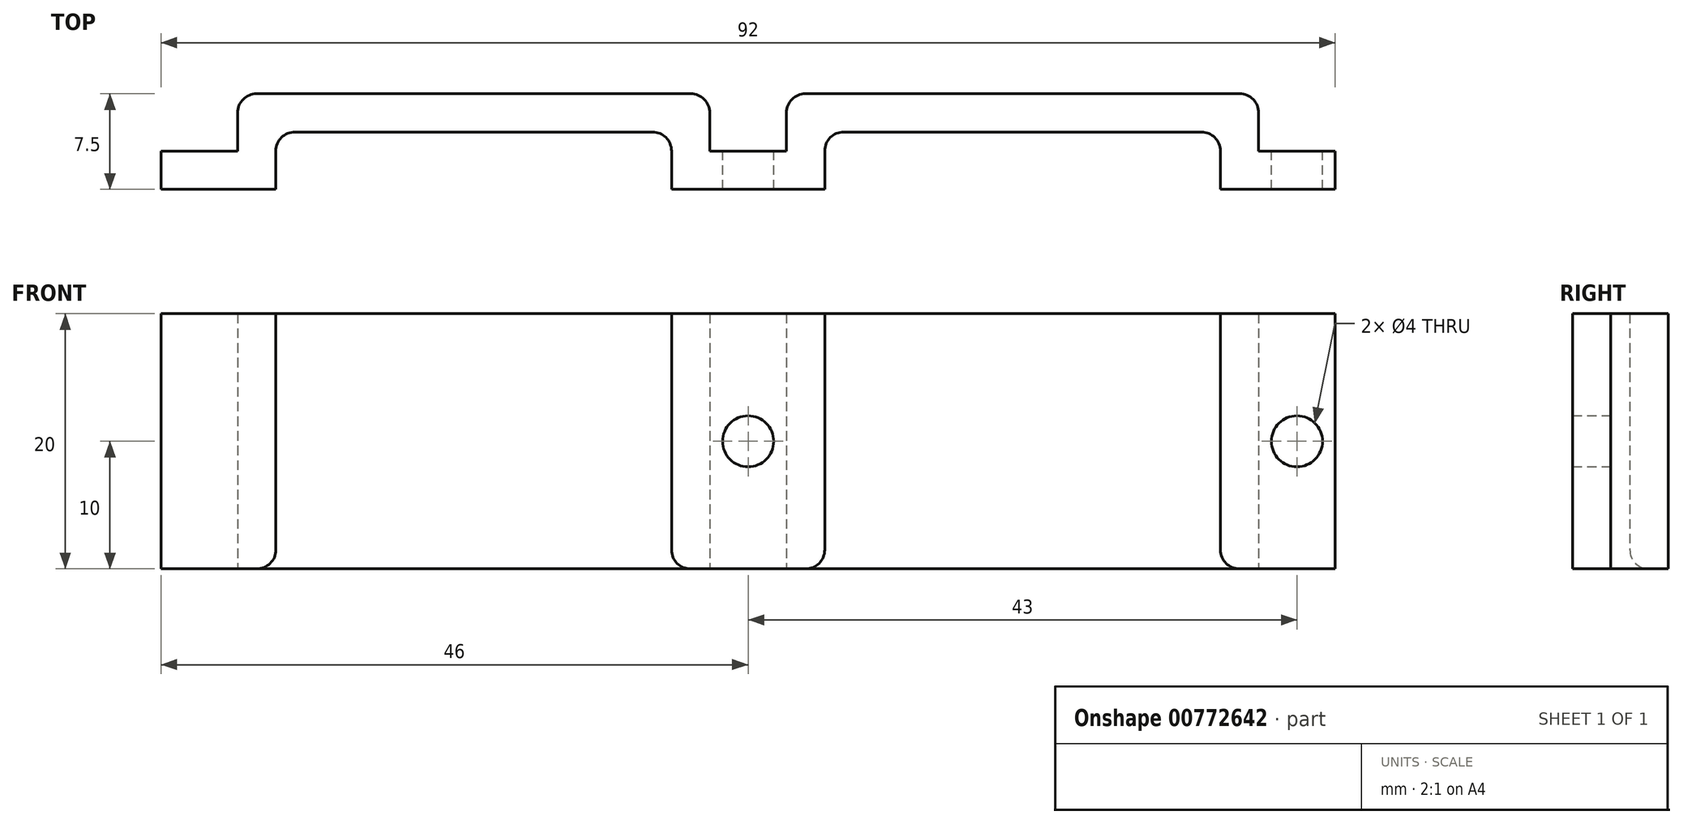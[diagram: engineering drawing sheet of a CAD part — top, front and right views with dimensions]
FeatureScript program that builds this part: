
annotation { "Feature Type Name" : "Feature", "Feature Type Description" : "" }
export const myFeature = defineFeature(function(context is Context, id is Id, definition is map)
    precondition{}
    {
        {
            var Q0;
            Q0=qCreatedBy(makeId("Top.planeOp"),FACE);
            var sketch = newSketch(context, id + "F0", { "sketchPlane" : qUnion([Q0])});
            skPoint(sketch, "E0.middle", {"position": v(0, 0) * mm});
            skLineSegment(sketch, "E1", {"start": v(-37, -4) * mm, "end": v(-37, 0.5) * mm});
            skLineSegment(sketch, "E2", {"start": v(-37, 0.5) * mm, "end": v(-6, 0.5) * mm});
            skLineSegment(sketch, "E3", {"start": v(-6, 0.5) * mm, "end": v(-6, -4) * mm});
            skLineSegment(sketch, "E4", {"start": v(-3, -1) * mm, "end": v(0, -1) * mm});
            skLineSegment(sketch, "E5", {"start": v(-40, -4) * mm, "end": v(-46, -4) * mm});
            skLineSegment(sketch, "E6", {"start": v(-46, -4) * mm, "end": v(-46, -1) * mm});
            skLineSegment(sketch, "E7", {"start": v(-46, -1) * mm, "end": v(-40, -1) * mm});
            skLineSegment(sketch, "E8", {"start": v(-40, -1) * mm, "end": v(-40, 3.5) * mm});
            skLineSegment(sketch, "E9", {"start": v(-40, 3.5) * mm, "end": v(-3, 3.5) * mm});
            skLineSegment(sketch, "E10", {"start": v(-3, -1) * mm, "end": v(-3, 3.5) * mm});
            skPoint(sketch, "E11.orphan", {"position": v(0, 3.5) * mm});
            skLineSegment(sketch, "E12.trimOffspring", {"start": v(-37, -4) * mm, "end": v(-40, -4) * mm});
            skLineSegment(sketch, "E13.MirrorCS", {"start": v(3, -1) * mm, "end": v(0, -1) * mm});
            skLineSegment(sketch, "E14.MirrorCS", {"start": v(3, -1) * mm, "end": v(3, 3.5) * mm});
            skLineSegment(sketch, "E15.MirrorCS", {"start": v(40, 3.5) * mm, "end": v(3, 3.5) * mm});
            skLineSegment(sketch, "E16.MirrorCS", {"start": v(40, -1) * mm, "end": v(40, 3.5) * mm});
            skLineSegment(sketch, "E17.MirrorCS", {"start": v(46, -1) * mm, "end": v(40, -1) * mm});
            skLineSegment(sketch, "E18.MirrorCS", {"start": v(46, -4) * mm, "end": v(46, -1) * mm});
            skLineSegment(sketch, "E19.MirrorCS", {"start": v(40, -4) * mm, "end": v(46, -4) * mm});
            skLineSegment(sketch, "E20.MirrorCS", {"start": v(37, -4) * mm, "end": v(40, -4) * mm});
            skLineSegment(sketch, "E21.MirrorCS", {"start": v(37, -4) * mm, "end": v(37, 0.5) * mm});
            skLineSegment(sketch, "E22.MirrorCS", {"start": v(37, 0.5) * mm, "end": v(6, 0.5) * mm});
            skLineSegment(sketch, "E23.MirrorCS", {"start": v(6, 0.5) * mm, "end": v(6, -4) * mm});
            skLineSegment(sketch, "E24", {"start": v(-6, -4) * mm, "end": v(6, -4) * mm});
            skSolve(sketch);
        }
        {
            var Q0;
            Q0=makeQuery(id+"F0.imprint","IMPRINT",FACE,{"disambiguationData":[TD([[makeQuery(id+"F0.imprint","IMPRINT",EDGE,{"derivedFrom":sQuery(id+"F0.wireOp",EDGE,"E1")}),1.0]])]});
            extrude(context, id + "F1", {"entities" : qUnion([Q0]), "depth" : 20 * mm, "offsetDistance" : 25 * mm});
        }
        {
            var Q0;
            Q0=makeQuery(id+"F1.opExtrude","CAP_EDGE",EDGE,{"disambiguationData":[OSD([sQuery(id+"F0.wireOp",EDGE,"E2")])],"isStart":true});
            var Q1;
            Q1=makeQuery(id+"F1.opExtrude","CAP_EDGE",EDGE,{"disambiguationData":[OSD([sQuery(id+"F0.wireOp",EDGE,"E1")])],"isStart":true});
            var Q2;
            Q2=makeQuery(id+"F1.opExtrude","CAP_EDGE",EDGE,{"disambiguationData":[OSD([sQuery(id+"F0.wireOp",EDGE,"E3")])],"isStart":true});
            var Q3;
            Q3=makeQuery(id+"F1.opExtrude","CAP_EDGE",EDGE,{"disambiguationData":[OSD([sQuery(id+"F0.wireOp",EDGE,"E23.MirrorCS")])],"isStart":true});
            var Q4;
            Q4=makeQuery(id+"F1.opExtrude","CAP_EDGE",EDGE,{"disambiguationData":[OSD([sQuery(id+"F0.wireOp",EDGE,"E22.MirrorCS")])],"isStart":true});
            var Q5;
            Q5=makeQuery(id+"F1.opExtrude","CAP_EDGE",EDGE,{"disambiguationData":[OSD([sQuery(id+"F0.wireOp",EDGE,"E21.MirrorCS")])],"isStart":true});
            var Q6;
            Q6=makeQuery(id+"F1.opExtrude","SWEPT_EDGE",EDGE,{"disambiguationData":[OSD([sQuery(id+"F0.wireOp",EDGE,"E8"),sQuery(id+"F0.wireOp",EDGE,"E9")])]});
            var Q7;
            Q7=makeQuery(id+"F1.opExtrude","SWEPT_EDGE",EDGE,{"disambiguationData":[OSD([sQuery(id+"F0.wireOp",EDGE,"E9"),sQuery(id+"F0.wireOp",EDGE,"E10")])]});
            var Q8;
            Q8=makeQuery(id+"F1.opExtrude","SWEPT_EDGE",EDGE,{"disambiguationData":[OSD([sQuery(id+"F0.wireOp",EDGE,"E14.MirrorCS"),sQuery(id+"F0.wireOp",EDGE,"E15.MirrorCS")])]});
            var Q9;
            Q9=makeQuery(id+"F1.opExtrude","SWEPT_EDGE",EDGE,{"disambiguationData":[OSD([sQuery(id+"F0.wireOp",EDGE,"E15.MirrorCS"),sQuery(id+"F0.wireOp",EDGE,"E16.MirrorCS")])]});
            var Q10;
            Q10=makeQuery(id+"F1.opExtrude","SWEPT_EDGE",EDGE,{"disambiguationData":[OSD([sQuery(id+"F0.wireOp",EDGE,"E1"),sQuery(id+"F0.wireOp",EDGE,"E2")])]});
            var Q11;
            Q11=makeQuery(id+"F1.opExtrude","SWEPT_EDGE",EDGE,{"disambiguationData":[OSD([sQuery(id+"F0.wireOp",EDGE,"E2"),sQuery(id+"F0.wireOp",EDGE,"E3")])]});
            var Q12;
            Q12=makeQuery(id+"F1.opExtrude","SWEPT_EDGE",EDGE,{"disambiguationData":[OSD([sQuery(id+"F0.wireOp",EDGE,"E22.MirrorCS"),sQuery(id+"F0.wireOp",EDGE,"E23.MirrorCS")])]});
            var Q13;
            Q13=makeQuery(id+"F1.opExtrude","SWEPT_EDGE",EDGE,{"disambiguationData":[OSD([sQuery(id+"F0.wireOp",EDGE,"E21.MirrorCS"),sQuery(id+"F0.wireOp",EDGE,"E22.MirrorCS")])]});
            fillet(context, id + "F2", {"entities" : qUnion([Q0, Q1, Q2, Q3, Q4, Q5, Q6, Q7, Q8, Q9, Q10, Q11, Q12, Q13]), "radius" : 1.5 * mm, "tangentPropagation" : true, "allowEdgeOverflow" : false});
        }
        {
            var Q0;
            Q0=makeQuery(id+"F1.opExtrude","SWEPT_FACE",FACE,{"disambiguationData":[OSD([sQuery(id+"F0.wireOp",EDGE,"E4"),sQuery(id+"F0.wireOp",EDGE,"E13.MirrorCS")])]});
            var sketch = newSketch(context, id + "F3", { "sketchPlane" : qUnion([Q0])});
            skCircle(sketch, "E25", {"center": v(0, 10) * mm, "radius": 2 * mm});
            skCircle(sketch, "E26", {"center": v(-43, 10) * mm, "radius": 2 * mm});
            skCircle(sketch, "E27.MirrorC", {"center": v(43, 10) * mm, "radius": 2 * mm});
            skSolve(sketch);
        }
        {
            var Q0;
            Q0=makeQuery(id+"F3.imprint","IMPRINT",FACE,{"disambiguationData":[TD([[makeQuery(id+"F3.imprint","IMPRINT",EDGE,{"derivedFrom":sQuery(id+"F3.wireOp",EDGE,"E26")}),1.0]])]});
            var Q1;
            Q1=makeQuery(id+"F3.imprint","IMPRINT",FACE,{"disambiguationData":[TD([[makeQuery(id+"F3.imprint","IMPRINT",EDGE,{"derivedFrom":sQuery(id+"F3.wireOp",EDGE,"E25")}),1.0]])]});
            var Q2;
            Q2=makeQuery(id+"F3.imprint","IMPRINT",FACE,{"disambiguationData":[TD([[makeQuery(id+"F3.imprint","IMPRINT",EDGE,{"derivedFrom":sQuery(id+"F3.wireOp",EDGE,"E27.MirrorC")}),-1.0]])]});
            extrude(context, id + "F4", {"entities" : qUnion([Q0, Q1, Q2]), "operationType" : NewBodyOperationType.REMOVE, "oppositeDirection" : true, "depth" : 25 * mm, "offsetDistance" : 25 * mm});
        }
    });
